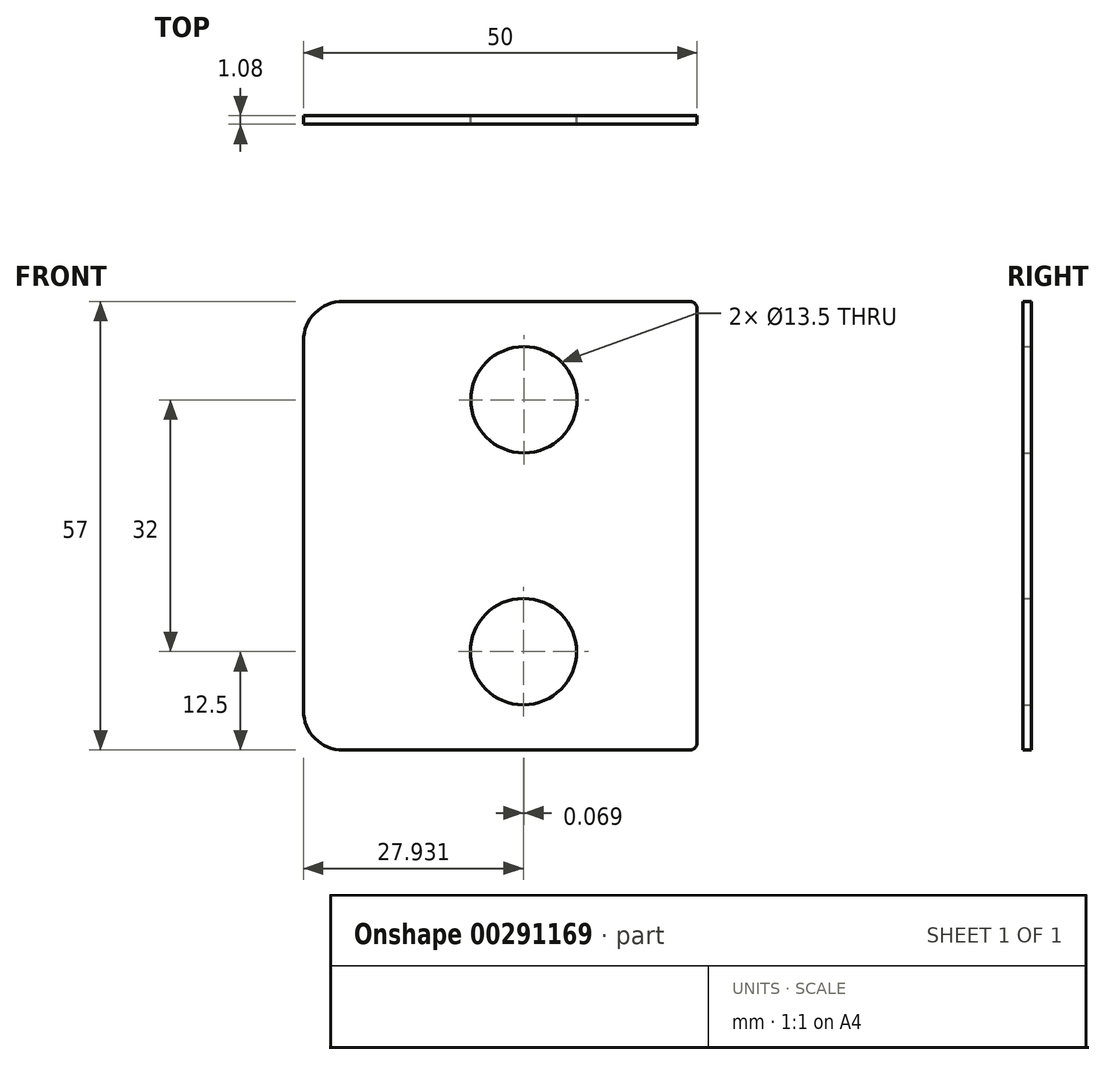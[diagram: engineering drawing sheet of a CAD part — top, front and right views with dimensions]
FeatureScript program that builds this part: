
annotation { "Feature Type Name" : "Feature", "Feature Type Description" : "" }
export const myFeature = defineFeature(function(context is Context, id is Id, definition is map)
    precondition{}
    {
        {
            var Q0;
            Q0=qCreatedBy(makeId("Front.planeOp"),FACE);
            var sketch = newSketch(context, id + "F0", { "sketchPlane" : qUnion([Q0])});
            skLineSegment(sketch, "E0.bottom", {"start": v(-1, 0) * mm, "end": v(-45, 0) * mm});
            skLineSegment(sketch, "E0.top", {"start": v(-1, 57) * mm, "end": v(-45, 57) * mm});
            skLineSegment(sketch, "E0.left", {"start": v(0, 1) * mm, "end": v(0, 56) * mm});
            skLineSegment(sketch, "E0.right", {"start": v(-50, 5) * mm, "end": v(-50, 52) * mm});
            skPoint(sketch, "E1.visualSharp", {"position": v(-50, 57) * mm});
            skArc(sketch, "E1.filletArc", {"start": v(-45, 57) * mm, "mid": v(-48.54, 55.54) * mm, "end": v(-50, 52) * mm});
            skPoint(sketch, "E2.visualSharp", {"position": v(-50, 0) * mm});
            skArc(sketch, "E2.filletArc", {"start": v(-50, 5) * mm, "mid": v(-48.54, 1.46) * mm, "end": v(-45, 0) * mm});
            skPoint(sketch, "E3.visualSharp", {"position": v(0, 0) * mm});
            skArc(sketch, "E3.filletArc", {"start": v(-1, 0) * mm, "mid": v(-0.3, 0.3) * mm, "end": v(0, 1) * mm});
            skPoint(sketch, "E4.visualSharp", {"position": v(0, 57) * mm});
            skArc(sketch, "E4.filletArc", {"start": v(0, 56) * mm, "mid": v(-0.3, 56.7) * mm, "end": v(-1, 57) * mm});
            skSolve(sketch);
        }
        {
            var Q0;
            Q0=makeQuery(id+"F0.imprint","IMPRINT",FACE,{"disambiguationData":[TD([[makeQuery(id+"F0.imprint","IMPRINT",EDGE,{"derivedFrom":sQuery(id+"F0.wireOp",EDGE,"E0.bottom")}),-1.0]])]});
            extrude(context, id + "F1", {"entities" : qUnion([Q0]), "depth" : 1.08 * mm});
        }
        {
            var Q0;
            Q0=makeQuery(id+"F1.opExtrude","CAP_FACE",FACE,{"disambiguationData":[OSD([sQuery(id+"F0.wireOp",EDGE,"E0.bottom"),sQuery(id+"F0.wireOp",EDGE,"E0.top"),sQuery(id+"F0.wireOp",EDGE,"E0.left"),sQuery(id+"F0.wireOp",EDGE,"E0.right"),sQuery(id+"F0.wireOp",EDGE,"E1.filletArc"),sQuery(id+"F0.wireOp",EDGE,"E2.filletArc"),sQuery(id+"F0.wireOp",EDGE,"E3.filletArc"),sQuery(id+"F0.wireOp",EDGE,"E4.filletArc")])],"isStart":false});
            var sketch = newSketch(context, id + "F2", { "sketchPlane" : qUnion([Q0])});
            skCircle(sketch, "E5", {"center": v(-22, 44.5) * mm, "radius": 6.75 * mm});
            skCircle(sketch, "E6", {"center": v(-22.07, 12.5) * mm, "radius": 6.75 * mm});
            skSolve(sketch);
        }
        {
            var Q0;
            Q0=sQuery(id+"F2.wireOp",VERTEX,"E5.center");
            var Q1;
            Q1=sQuery(id+"F2.wireOp",VERTEX,"E6.center");
            var Q2;
            Q2=makeQuery(id+"F1.opExtrude","SWEPT_BODY",BODY,{"disambiguationData":[OSD([sQuery(id+"F0.wireOp",EDGE,"E0.bottom"),sQuery(id+"F0.wireOp",EDGE,"E0.top"),sQuery(id+"F0.wireOp",EDGE,"E0.left"),sQuery(id+"F0.wireOp",EDGE,"E0.right"),sQuery(id+"F0.wireOp",EDGE,"E1.filletArc"),sQuery(id+"F0.wireOp",EDGE,"E2.filletArc"),sQuery(id+"F0.wireOp",EDGE,"E3.filletArc"),sQuery(id+"F0.wireOp",EDGE,"E4.filletArc")])]});
            hole(context, id + "F3", {"style" : HoleStyle.SIMPLE, "endStyle" : HoleEndStyle.THROUGH, "holeDiameter" : 13.5 * mm, "tappedDepth" : 10 * mm, "tapClearance" : 3, "locations" : qUnion([Q0, Q1]), "scope" : qUnion([Q2]), "startStyle" : HoleStartStyle.PART});
        }
    });
